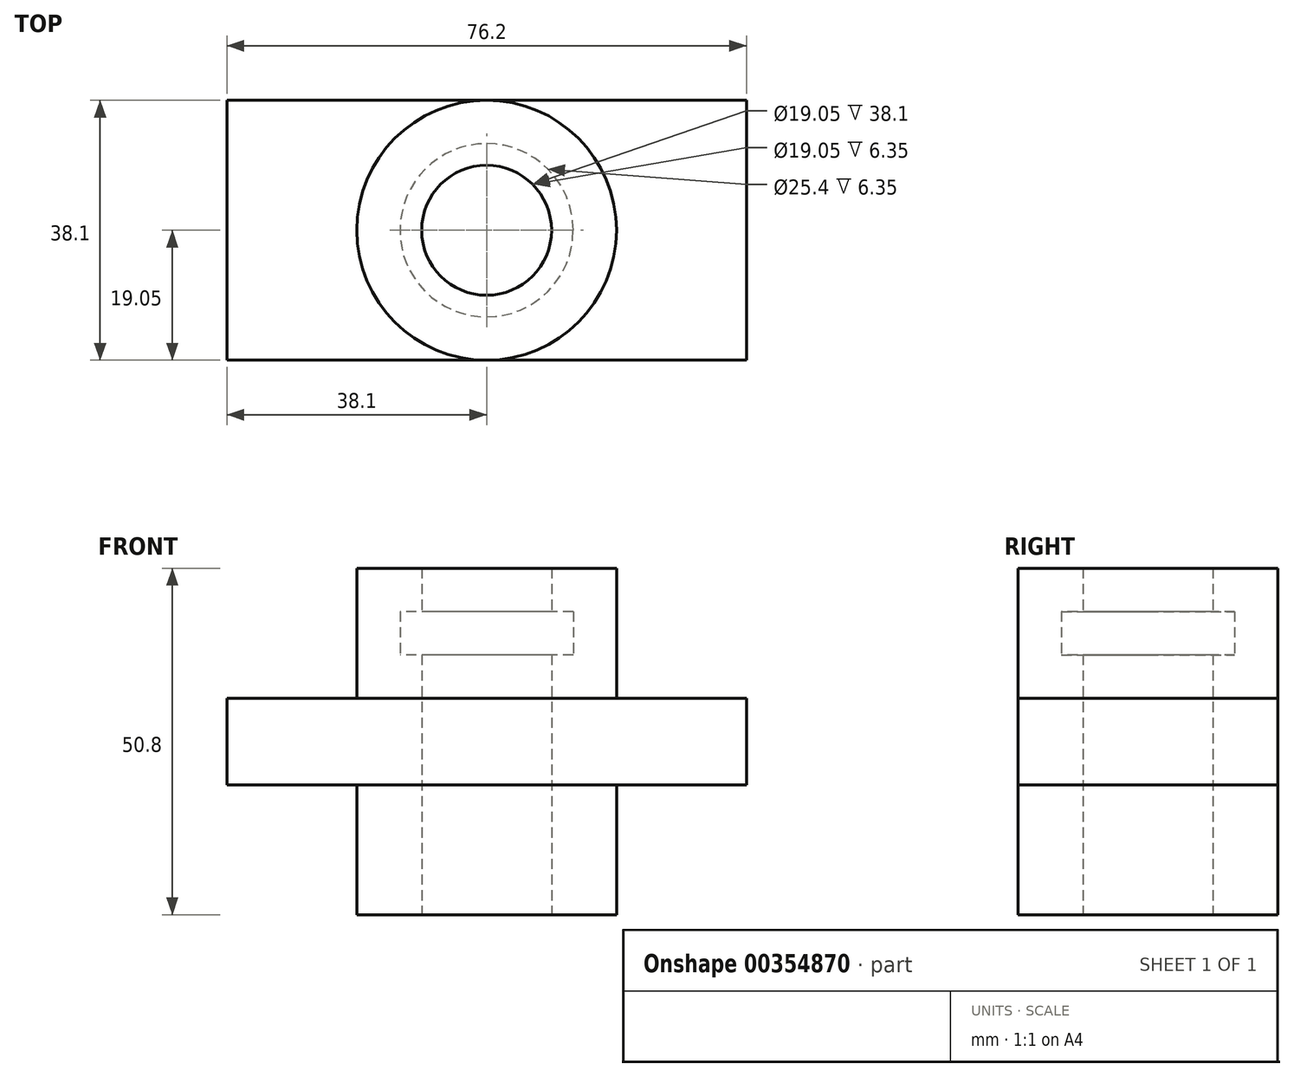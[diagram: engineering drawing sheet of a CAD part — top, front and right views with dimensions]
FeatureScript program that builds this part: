
annotation { "Feature Type Name" : "Feature", "Feature Type Description" : "" }
export const myFeature = defineFeature(function(context is Context, id is Id, definition is map)
    precondition{}
    {
        {
            var Q0;
            Q0=qCreatedBy(makeId("Top.planeOp"),FACE);
            var sketch = newSketch(context, id + "F0", { "sketchPlane" : qUnion([Q0])});
            skCircle(sketch, "E0", {"center": v(0, 0) * mm, "radius": 9.53 * mm});
            skCircle(sketch, "E1", {"center": v(0, 0) * mm, "radius": 19.05 * mm});
            skLineSegment(sketch, "E2.left", {"start": v(-38.1, 19.05) * mm, "end": v(-38.1, -19.05) * mm});
            skLineSegment(sketch, "E2.right", {"start": v(38.1, 19.05) * mm, "end": v(38.1, -19.05) * mm});
            skLineSegment(sketch, "E3", {"start": v(-38.1, 19.05) * mm, "end": v(0, 19.05) * mm});
            skLineSegment(sketch, "E4", {"start": v(0, 19.05) * mm, "end": v(38.1, 19.05) * mm});
            skLineSegment(sketch, "E5", {"start": v(-38.1, -19.05) * mm, "end": v(0, -19.05) * mm});
            skLineSegment(sketch, "E6", {"start": v(0, -19.05) * mm, "end": v(38.1, -19.05) * mm});
            skSolve(sketch);
        }
        {
            var Q0;
            Q0=makeQuery(id+"F0.imprint","IMPRINT",FACE,{"disambiguationData":[TD([[makeQuery(id+"F0.imprint","IMPRINT",EDGE,{"derivedFrom":sQuery(id+"F0.wireOp",EDGE,"E0")}),-1.0]])]});
            var Q1;
            Q1=makeQuery(id+"F0.imprint","IMPRINT",FACE,{"disambiguationData":[TD([[makeQuery(id+"F0.imprint","IMPRINT",EDGE,{"derivedFrom":sQuery(id+"F0.wireOp",EDGE,"E2.right")}),-1.0]])]});
            var Q2;
            Q2=makeQuery(id+"F0.imprint","IMPRINT",FACE,{"disambiguationData":[TD([[makeQuery(id+"F0.imprint","IMPRINT",EDGE,{"derivedFrom":sQuery(id+"F0.wireOp",EDGE,"E2.left")}),1.0]])]});
            extrude(context, id + "F1", {"entities" : qUnion([Q0, Q1, Q2]), "endBound" : BoundingType.SYMMETRIC, "depth" : 12.7 * mm});
        }
        {
            var Q0;
            Q0=makeQuery(id+"F0.imprint","IMPRINT",FACE,{"disambiguationData":[TD([[makeQuery(id+"F0.imprint","IMPRINT",EDGE,{"derivedFrom":sQuery(id+"F0.wireOp",EDGE,"E0")}),-1.0]])]});
            extrude(context, id + "F2", {"entities" : qUnion([Q0]), "operationType" : NewBodyOperationType.ADD, "oppositeDirection" : true, "depth" : 25.4 * mm, "hasSecondDirection" : true, "secondDirectionOppositeDirection" : false, "secondDirectionDepth" : 12.7 * mm});
        }
        {
            var Q0;
            Q0=makeQuery(id+"F2.opExtrude","CAP_FACE",FACE,{"disambiguationData":[OSD([sQuery(id+"F0.wireOp",EDGE,"E0"),sQuery(id+"F0.wireOp",EDGE,"E1")])],"isStart":true});
            var sketch = newSketch(context, id + "F3", { "sketchPlane" : qUnion([Q0])});
            skCircle(sketch, "E7", {"center": v(0, 0) * mm, "radius": 12.7 * mm});
            skCircle(sketch, "E8.0", {"center": v(0, 0) * mm, "radius": 9.53 * mm});
            skCircle(sketch, "E9.0", {"center": v(0, 0) * mm, "radius": 19.05 * mm});
            skSolve(sketch);
        }
        {
            var Q0;
            Q0 = qSketchRegion(id + "F3", true);
            var Q1;
            Q1=makeQuery(id+"F3.imprint","IMPRINT",FACE,{"disambiguationData":[TD([[makeQuery(id+"F3.imprint","IMPRINT",EDGE,{"derivedFrom":sQuery(id+"F3.wireOp",EDGE,"E7")}),1.0]])]});
            extrude(context, id + "F4", {"entities" : qUnion([Q0, Q1]), "operationType" : NewBodyOperationType.ADD, "depth" : 12.7 * mm});
        }
        {
            var Q0;
            Q0=makeQuery(id+"F3.imprint","IMPRINT",FACE,{"disambiguationData":[TD([[makeQuery(id+"F3.imprint","IMPRINT",EDGE,{"derivedFrom":sQuery(id+"F3.wireOp",EDGE,"E7")}),1.0]])]});
            extrude(context, id + "F5", {"entities" : qUnion([Q0]), "operationType" : NewBodyOperationType.REMOVE, "depth" : 6.35 * mm});
        }
    });
